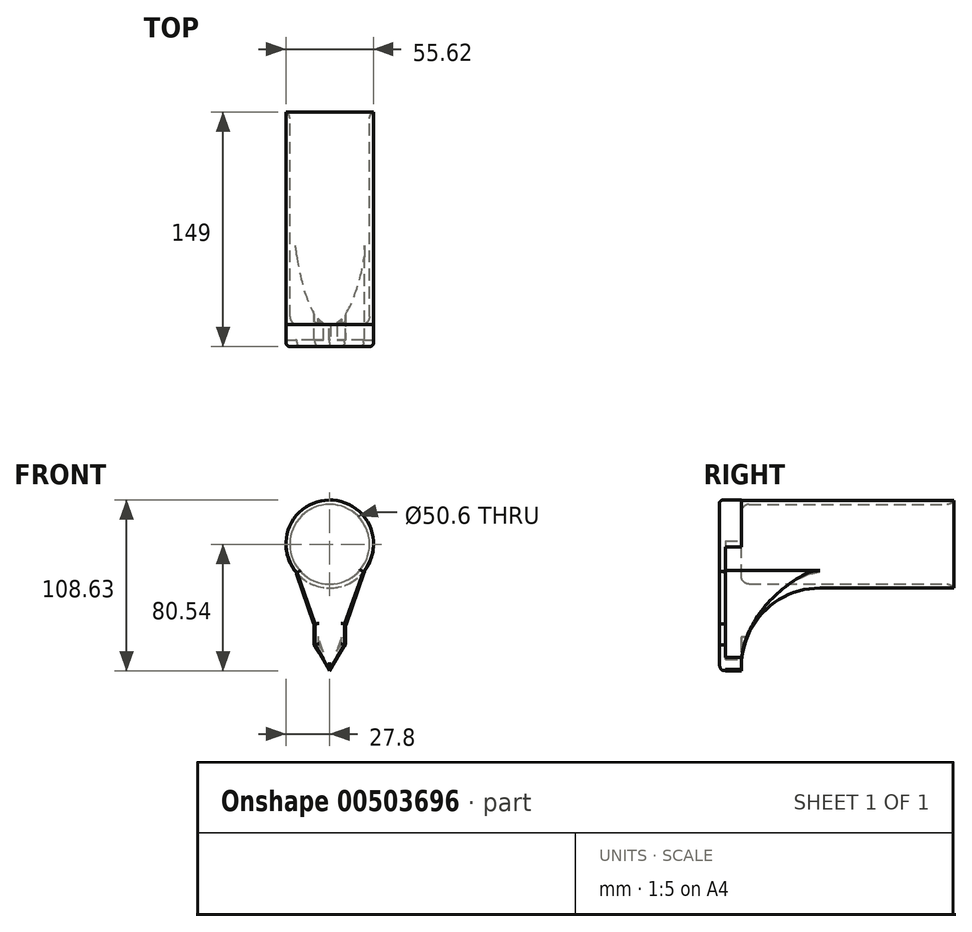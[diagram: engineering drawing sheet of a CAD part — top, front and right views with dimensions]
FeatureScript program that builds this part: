
annotation { "Feature Type Name" : "Feature", "Feature Type Description" : "" }
export const myFeature = defineFeature(function(context is Context, id is Id, definition is map)
    precondition{}
    {
        {
            var Q0;
            Q0=qCreatedBy(makeId("Front.planeOp"),FACE);
            var sketch = newSketch(context, id + "F0", { "sketchPlane" : qUnion([Q0])});
            skCircle(sketch, "E0", {"center": v(0, 0) * mm, "radius": 25.3 * mm});
            skCircle(sketch, "E1.0", {"center": v(0, 0) * mm, "radius": 27.8 * mm});
            skLineSegment(sketch, "E2", {"start": v(0, 20.72) * mm, "end": v(0, -79.2) * mm});
            skLineSegment(sketch, "E3", {"start": v(0, -79.2) * mm, "end": v(10, -64.06) * mm});
            skLineSegment(sketch, "E4", {"start": v(10, -64.06) * mm, "end": v(10, 25.94) * mm});
            skLineSegment(sketch, "E5", {"start": v(-10, 25.94) * mm, "end": v(-10, -64.06) * mm});
            skLineSegment(sketch, "E6", {"start": v(-10, -64.06) * mm, "end": v(0, -79.2) * mm});
            skLineSegment(sketch, "E7", {"start": v(-10, 25.94) * mm, "end": v(10, 25.94) * mm});
            skLineSegment(sketch, "E8", {"start": v(0, 20.72) * mm, "end": v(10, 25.94) * mm});
            skLineSegment(sketch, "E9", {"start": v(0, 20.72) * mm, "end": v(-10, 25.94) * mm});
            skLineSegment(sketch, "E10", {"start": v(10, -64.06) * mm, "end": v(0, -64.06) * mm});
            skLineSegment(sketch, "E11", {"start": v(0, -64.06) * mm, "end": v(-10, -64.06) * mm});
            skLineSegment(sketch, "E12", {"start": v(10, -30.76) * mm, "end": v(-10, -30.76) * mm});
            skSolve(sketch);
        }
        {
            var Q0;
            Q0 = qSketchRegion(id + "F0", true);
            var Q1;
            {var subQ1=sQuery(id+"F0.wireOp",EDGE,"E0");var subQ6=sQuery(id+"F0.wireOp",EDGE,"E9");var subQ8=makeQuery(id+"F0.imprint","INTERSECT",VERTEX,{"derivedFrom":[subQ1,subQ6]});Q1=makeQuery(id+"F0.imprint","IMPRINT",FACE,{"disambiguationData":[TD([[makeQuery(id+"F0.imprint","IMPRINT",EDGE,{"disambiguationData":[TD([[subQ8,-1.0]])],"derivedFrom":subQ1}),1.0]])]});}
            var Q2;
            {var subQ1=sQuery(id+"F0.wireOp",EDGE,"E0");var subQ4=sQuery(id+"F0.wireOp",EDGE,"E8");var subQ8=makeQuery(id+"F0.imprint","INTERSECT",VERTEX,{"derivedFrom":[subQ1,subQ4]});Q2=makeQuery(id+"F0.imprint","IMPRINT",FACE,{"disambiguationData":[TD([[makeQuery(id+"F0.imprint","IMPRINT",EDGE,{"disambiguationData":[TD([[subQ8,1.0]])],"derivedFrom":subQ1}),1.0]])]});}
            extrude(context, id + "F1", {"entities" : qUnion([Q0, Q1, Q2]), "depth" : 10 * mm});
        }
        {
            var Q0;
            Q0=makeQuery(id+"F1.opExtrude","CAP_FACE",FACE,{"disambiguationData":[OSD([sQuery(id+"F0.wireOp",EDGE,"E0"),sQuery(id+"F0.wireOp",EDGE,"E1.0"),sQuery(id+"F0.wireOp",EDGE,"E3"),sQuery(id+"F0.wireOp",EDGE,"E4"),sQuery(id+"F0.wireOp",EDGE,"E5"),sQuery(id+"F0.wireOp",EDGE,"E6"),sQuery(id+"F0.wireOp",EDGE,"E8"),sQuery(id+"F0.wireOp",EDGE,"E9")])],"isStart":true});
            shell(context, id + "F2", {"entities" : qUnion([Q0]), "thickness" : 2.5 * mm});
        }
        {
            var Q0;
            Q0=qCreatedBy(makeId("Front.planeOp"),FACE);
            var sketch = newSketch(context, id + "F3", { "sketchPlane" : qUnion([Q0])});
            skCircle(sketch, "E13", {"center": v(0, 0) * mm, "radius": 25.3 * mm});
            skCircle(sketch, "E14.0", {"center": v(0, 0) * mm, "radius": 27.8 * mm});
            skSolve(sketch);
        }
        {
            var Q0;
            Q0 = qSketchRegion(id + "F3", true);
            extrude(context, id + "F4", {"entities" : qUnion([Q0]), "operationType" : NewBodyOperationType.ADD, "oppositeDirection" : true, "depth" : 135 * mm});
        }
        {
            var Q0;
            Q0=qCreatedBy(makeId("Front.planeOp"),FACE);
            var sketch = newSketch(context, id + "F5", { "sketchPlane" : qUnion([Q0])});
            skCircle(sketch, "E15", {"center": v(0, 0) * mm, "radius": 27.1 * mm});
            skSolve(sketch);
        }
        {
            var Q0;
            Q0 = qSketchRegion(id + "F5", true);
            extrude(context, id + "F6", {"entities" : qUnion([Q0]), "operationType" : NewBodyOperationType.ADD, "depth" : 10 * mm});
        }
        {
            var Q0;
            Q0=qCreatedBy(makeId("Front.planeOp"),FACE);
            var sketch = newSketch(context, id + "F7", { "sketchPlane" : qUnion([Q0])});
            skLineSegment(sketch, "E16", {"start": v(22.34, -16.76) * mm, "end": v(0, -80.54) * mm});
            skLineSegment(sketch, "E17", {"start": v(0, -80.54) * mm, "end": v(-21.62, -16.76) * mm});
            skLineSegment(sketch, "E18", {"start": v(-21.62, -16.76) * mm, "end": v(22.34, -16.76) * mm});
            skSolve(sketch);
        }
        {
            var Q0;
            Q0 = qSketchRegion(id + "F7", true);
            extrude(context, id + "F8", {"entities" : qUnion([Q0]), "operationType" : NewBodyOperationType.ADD, "depth" : 10 * mm});
        }
        {
            var Q0;
            {var subQ0=sQuery(id+"F0.wireOp",EDGE,"E1.0");var subQ1=makeQuery(id+"F1.opExtrude","SWEPT_FACE",FACE,{"disambiguationData":[OSD([subQ0])]});var subQ2=sQuery(id+"F3.wireOp",EDGE,"E14.0");var subQ3=makeQuery(id+"F4.opExtrude","CAP_FACE",FACE,{"disambiguationData":[OSD([sQuery(id+"F3.wireOp",EDGE,"E13"),subQ2])],"isStart":true});var subQ4=makeQuery(id+"F4.opExtrude","SWEPT_FACE",FACE,{"disambiguationData":[OSD([subQ2])]});var subQ5=makeQuery(id+"F4.opExtrude","CAP_EDGE",EDGE,{"disambiguationData":[OSD([subQ2])],"isStart":true});var subQ6=sQuery(id+"F0.wireOp",EDGE,"E4");var subQ9=sQuery(id+"F0.wireOp",EDGE,"E3");var subQ10=sQuery(id+"F0.wireOp",EDGE,"E6");var subQ11=sQuery(id+"F0.wireOp",EDGE,"E5");var subQ12=makeQuery(id+"F1.opExtrude","CAP_FACE",FACE,{"disambiguationData":[OSD([sQuery(id+"F0.wireOp",EDGE,"E0"),subQ0,subQ9,subQ6,subQ11,subQ10,sQuery(id+"F0.wireOp",EDGE,"E8"),sQuery(id+"F0.wireOp",EDGE,"E9")])],"isStart":true});Q0=makeQuery(id+"F8.boolean.opBoolean","MERGE",EDGE,{"derivedFrom":[makeQuery(id+"F4.boolean.opBoolean","SPLIT",EDGE,{"disambiguationData":[topologyDisambiguationEdgeConnected([subQ12,subQ1,subQ4]),TD([makeQuery(id+"F2.opShell","OFFSET_FACE",FACE,{"disambiguationData":[OSD([subQ11])]})])],"derivedFrom":subQ5}),makeQuery(id+"F4.boolean.opBoolean","SPLIT",EDGE,{"disambiguationData":[topologyDisambiguationEdgeConnected([subQ12,subQ1,subQ4]),TD([makeQuery(id+"F2.opShell","OFFSET_FACE",FACE,{"disambiguationData":[OSD([subQ6])]})])],"derivedFrom":subQ5}),makeQuery(id+"F4.boolean.opBoolean","SPLIT",EDGE,{"disambiguationData":[topologyDisambiguationEdgeConnected([subQ1,subQ3,subQ4])],"derivedFrom":subQ5})]});}
            fillet(context, id + "F9", {"entities" : qUnion([Q0]), "radius" : 50 * mm, "tangentPropagation" : true, "allowEdgeOverflow" : false});
        }
        {
            var Q0;
            Q0=makeQuery(id+"F8.boolean.opBoolean","INTERSECT",EDGE,{"derivedFrom":[makeQuery(id+"F1.opExtrude","SWEPT_FACE",FACE,{"disambiguationData":[OSD([sQuery(id+"F0.wireOp",EDGE,"E6")])]}),makeQuery(id+"F8.opExtrude","SWEPT_FACE",FACE,{"disambiguationData":[OSD([sQuery(id+"F7.wireOp",EDGE,"E17")])]})]});
            var Q1;
            Q1=makeQuery(id+"F1.opExtrude","SWEPT_EDGE",EDGE,{"disambiguationData":[OSD([sQuery(id+"F0.wireOp",EDGE,"E5"),sQuery(id+"F0.wireOp",EDGE,"E6"),sQuery(id+"F0.wireOp",EDGE,"E11")])]});
            var Q2;
            {var subQ0=sQuery(id+"F0.wireOp",EDGE,"E5");var subQ1=makeQuery(id+"F0.imprint","INTERSECT",VERTEX,{"derivedFrom":[subQ0,sQuery(id+"F0.wireOp",EDGE,"E12")]});Q2=makeQuery(id+"F8.boolean.opBoolean","INTERSECT",EDGE,{"derivedFrom":[makeQuery(id+"F1.opExtrude","SWEPT_FACE",FACE,{"disambiguationData":[OSD([subQ0]),TDD([makeQuery(id+"F0.imprint","IMPRINT",EDGE,{"disambiguationData":[TD([[subQ1,1.0]])],"derivedFrom":subQ0}),makeQuery(id+"F0.imprint","IMPRINT",EDGE,{"disambiguationData":[TD([[subQ1,-1.0]])],"derivedFrom":subQ0})])]}),makeQuery(id+"F8.opExtrude","SWEPT_FACE",FACE,{"disambiguationData":[OSD([sQuery(id+"F7.wireOp",EDGE,"E17")])]})]});}
            var Q3;
            Q3=makeQuery(id+"F8.boolean.opBoolean","INTERSECT",EDGE,{"derivedFrom":[makeQuery(id+"F4.boolean.opBoolean","MERGE",FACE,{"derivedFrom":[makeQuery(id+"F1.opExtrude","SWEPT_FACE",FACE,{"disambiguationData":[OSD([sQuery(id+"F0.wireOp",EDGE,"E1.0")])]}),makeQuery(id+"F4.opExtrude","SWEPT_FACE",FACE,{"disambiguationData":[OSD([sQuery(id+"F3.wireOp",EDGE,"E14.0")])]})]}),makeQuery(id+"F8.opExtrude","SWEPT_FACE",FACE,{"disambiguationData":[OSD([sQuery(id+"F7.wireOp",EDGE,"E17")])]})]});
            var Q4;
            Q4=makeQuery(id+"F8.boolean.opBoolean","INTERSECT",EDGE,{"derivedFrom":[makeQuery(id+"F1.opExtrude","SWEPT_FACE",FACE,{"disambiguationData":[OSD([sQuery(id+"F0.wireOp",EDGE,"E3")])]}),makeQuery(id+"F8.opExtrude","SWEPT_FACE",FACE,{"disambiguationData":[OSD([sQuery(id+"F7.wireOp",EDGE,"E16")])]})]});
            var Q5;
            Q5=makeQuery(id+"F1.opExtrude","SWEPT_EDGE",EDGE,{"disambiguationData":[OSD([sQuery(id+"F0.wireOp",EDGE,"E3"),sQuery(id+"F0.wireOp",EDGE,"E4"),sQuery(id+"F0.wireOp",EDGE,"E10")])]});
            var Q6;
            {var subQ0=sQuery(id+"F0.wireOp",EDGE,"E4");var subQ1=makeQuery(id+"F0.imprint","INTERSECT",VERTEX,{"derivedFrom":[subQ0,sQuery(id+"F0.wireOp",EDGE,"E12")]});Q6=makeQuery(id+"F8.boolean.opBoolean","INTERSECT",EDGE,{"derivedFrom":[makeQuery(id+"F1.opExtrude","SWEPT_FACE",FACE,{"disambiguationData":[OSD([subQ0]),TDD([makeQuery(id+"F0.imprint","IMPRINT",EDGE,{"disambiguationData":[TD([[subQ1,1.0]])],"derivedFrom":subQ0}),makeQuery(id+"F0.imprint","IMPRINT",EDGE,{"disambiguationData":[TD([[subQ1,-1.0]])],"derivedFrom":subQ0})])]}),makeQuery(id+"F8.opExtrude","SWEPT_FACE",FACE,{"disambiguationData":[OSD([sQuery(id+"F7.wireOp",EDGE,"E16")])]})]});}
            var Q7;
            Q7=makeQuery(id+"F8.opExtrude","SWEPT_EDGE",EDGE,{"disambiguationData":[OSD([sQuery(id+"F7.wireOp",EDGE,"E16"),sQuery(id+"F7.wireOp",EDGE,"E18")])]});
            fillet(context, id + "F10", {"entities" : qUnion([Q0, Q1, Q2, Q3, Q4, Q5, Q6, Q7]), "radius" : 5 * mm, "tangentPropagation" : true, "allowEdgeOverflow" : false});
        }
        {
            var Q0;
            Q0=qCreatedBy(makeId("Front.planeOp"),FACE);
            var sketch = newSketch(context, id + "F11", { "sketchPlane" : qUnion([Q0])});
            skArc(sketch, "E19.0", {"start": v(21.44, -17.43) * mm, "mid": v(-0.4, 28.08) * mm, "end": v(-20.86, -18.07) * mm});
            skLineSegment(sketch, "E20", {"start": v(-20.86, -18.07) * mm, "end": v(-9.33, -50.69) * mm});
            skLineSegment(sketch, "E21", {"start": v(-9.33, -50.69) * mm, "end": v(-9.33, -63.89) * mm});
            skLineSegment(sketch, "E22", {"start": v(-9.33, -63.89) * mm, "end": v(0, -80.1) * mm});
            skLineSegment(sketch, "E23", {"start": v(0, -80.1) * mm, "end": v(9.52, -63.89) * mm});
            skLineSegment(sketch, "E24", {"start": v(9.52, -63.89) * mm, "end": v(9.52, -50.69) * mm});
            skLineSegment(sketch, "E25", {"start": v(9.52, -50.69) * mm, "end": v(21.44, -17.43) * mm});
            skSolve(sketch);
        }
        {
            var Q0;
            Q0 = qSketchRegion(id + "F11", true);
            extrude(context, id + "F12", {"entities" : qUnion([Q0]), "operationType" : NewBodyOperationType.ADD, "depth" : 14 * mm});
        }
        {
            var Q0;
            Q0=makeQuery(id+"F12.opExtrude","CAP_FACE",FACE,{"disambiguationData":[OSD([sQuery(id+"F11.wireOp",EDGE,"E19.0"),sQuery(id+"F11.wireOp",EDGE,"E20"),sQuery(id+"F11.wireOp",EDGE,"E21"),sQuery(id+"F11.wireOp",EDGE,"E22"),sQuery(id+"F11.wireOp",EDGE,"E23"),sQuery(id+"F11.wireOp",EDGE,"E24"),sQuery(id+"F11.wireOp",EDGE,"E25")])],"isStart":false});
            fillet(context, id + "F13", {"entities" : qUnion([Q0]), "radius" : 2.5 * mm, "tangentPropagation" : true, "allowEdgeOverflow" : false});
        }
        {
            var Q0;
            Q0=makeQuery(id+"F4.opExtrude","CAP_EDGE",EDGE,{"disambiguationData":[OSD([sQuery(id+"F3.wireOp",EDGE,"E13")])],"isStart":false});
            fillet(context, id + "F14", {"entities" : qUnion([Q0]), "radius" : 5 * mm, "tangentPropagation" : true, "allowEdgeOverflow" : false});
        }
        {
            var Q0;
            {var subQ0=sQuery(id+"F3.wireOp",EDGE,"E13");var subQ1=makeQuery(id+"F4.opExtrude","SWEPT_FACE",FACE,{"disambiguationData":[OSD([subQ0])]});var subQ2=sQuery(id+"F0.wireOp",EDGE,"E4");var subQ3=sQuery(id+"F0.wireOp",EDGE,"E0");var subQ4=makeQuery(id+"F0.imprint","INTERSECT",VERTEX,{"disambiguationData":[OD(0.0)],"derivedFrom":[subQ3,subQ2]});var subQ6=makeQuery(id+"F1.opExtrude","SWEPT_FACE",FACE,{"disambiguationData":[OSD([subQ3]),TDD([makeQuery(id+"F0.imprint","IMPRINT",EDGE,{"disambiguationData":[TD([[subQ4,1.0]])],"derivedFrom":subQ3})])]});var subQ7=sQuery(id+"F0.wireOp",EDGE,"E5");var subQ8=makeQuery(id+"F0.imprint","INTERSECT",VERTEX,{"disambiguationData":[OD(0.0)],"derivedFrom":[subQ3,subQ7]});var subQ10=makeQuery(id+"F1.opExtrude","SWEPT_FACE",FACE,{"disambiguationData":[OSD([subQ3]),TDD([makeQuery(id+"F0.imprint","IMPRINT",EDGE,{"disambiguationData":[TD([[subQ8,-1.0]])],"derivedFrom":subQ3})])]});var subQ11=sQuery(id+"F0.wireOp",EDGE,"E8");var subQ12=sQuery(id+"F0.wireOp",EDGE,"E9");var subQ13=makeQuery(id+"F1.opExtrude","SWEPT_FACE",FACE,{"disambiguationData":[OSD([subQ3]),TDD([makeQuery(id+"F0.imprint","IMPRINT",EDGE,{"disambiguationData":[TD([[makeQuery(id+"F0.imprint","INTERSECT",VERTEX,{"derivedFrom":[subQ3,subQ11]}),-1.0]])],"derivedFrom":subQ3})])]});var subQ14=makeQuery(id+"F4.opExtrude","CAP_FACE",FACE,{"disambiguationData":[OSD([subQ0,sQuery(id+"F3.wireOp",EDGE,"E14.0")])],"isStart":true});var subQ15=makeQuery(id+"F4.opExtrude","CAP_EDGE",EDGE,{"disambiguationData":[OSD([subQ0])],"isStart":true});var subQ16=makeQuery(id+"F1.opExtrude","CAP_FACE",FACE,{"disambiguationData":[OSD([subQ3,sQuery(id+"F0.wireOp",EDGE,"E1.0"),sQuery(id+"F0.wireOp",EDGE,"E3"),subQ2,subQ7,sQuery(id+"F0.wireOp",EDGE,"E6"),subQ11,subQ12])],"isStart":true});Q0=makeQuery(id+"F6.boolean.opBoolean","MERGE",EDGE,{"derivedFrom":[makeQuery(id+"F4.boolean.opBoolean","SPLIT",EDGE,{"disambiguationData":[topologyDisambiguationEdgeConnected([subQ13,subQ16,subQ10,subQ6,subQ1]),TD([makeQuery(id+"F1.opExtrude","SWEPT_FACE",FACE,{"disambiguationData":[OSD([subQ11])]})])],"derivedFrom":subQ15}),makeQuery(id+"F4.boolean.opBoolean","SPLIT",EDGE,{"disambiguationData":[topologyDisambiguationEdgeConnected([subQ13,subQ16,subQ10,subQ6,subQ1]),TD([makeQuery(id+"F1.opExtrude","SWEPT_FACE",FACE,{"disambiguationData":[OSD([subQ12])]})])],"derivedFrom":subQ15}),makeQuery(id+"F4.boolean.opBoolean","SPLIT",EDGE,{"disambiguationData":[topologyDisambiguationEdgeConnected([subQ13,subQ16,subQ10,subQ6,subQ1]),TD([makeQuery(id+"F2.opShell","OFFSET_FACE",FACE,{"disambiguationData":[OSD([subQ7])]})])],"derivedFrom":subQ15}),makeQuery(id+"F4.boolean.opBoolean","SPLIT",EDGE,{"disambiguationData":[topologyDisambiguationEdgeConnected([subQ13,subQ16,subQ10,subQ6,subQ1]),TD([makeQuery(id+"F2.opShell","OFFSET_FACE",FACE,{"disambiguationData":[OSD([subQ2])]})])],"derivedFrom":subQ15}),makeQuery(id+"F4.boolean.opBoolean","SPLIT",EDGE,{"disambiguationData":[topologyDisambiguationEdgeConnected([subQ13,subQ10,subQ6,subQ1,subQ14])],"derivedFrom":subQ15})]});}
            fillet(context, id + "F15", {"entities" : qUnion([Q0]), "radius" : 5 * mm, "tangentPropagation" : true, "allowEdgeOverflow" : false});
        }
    });
